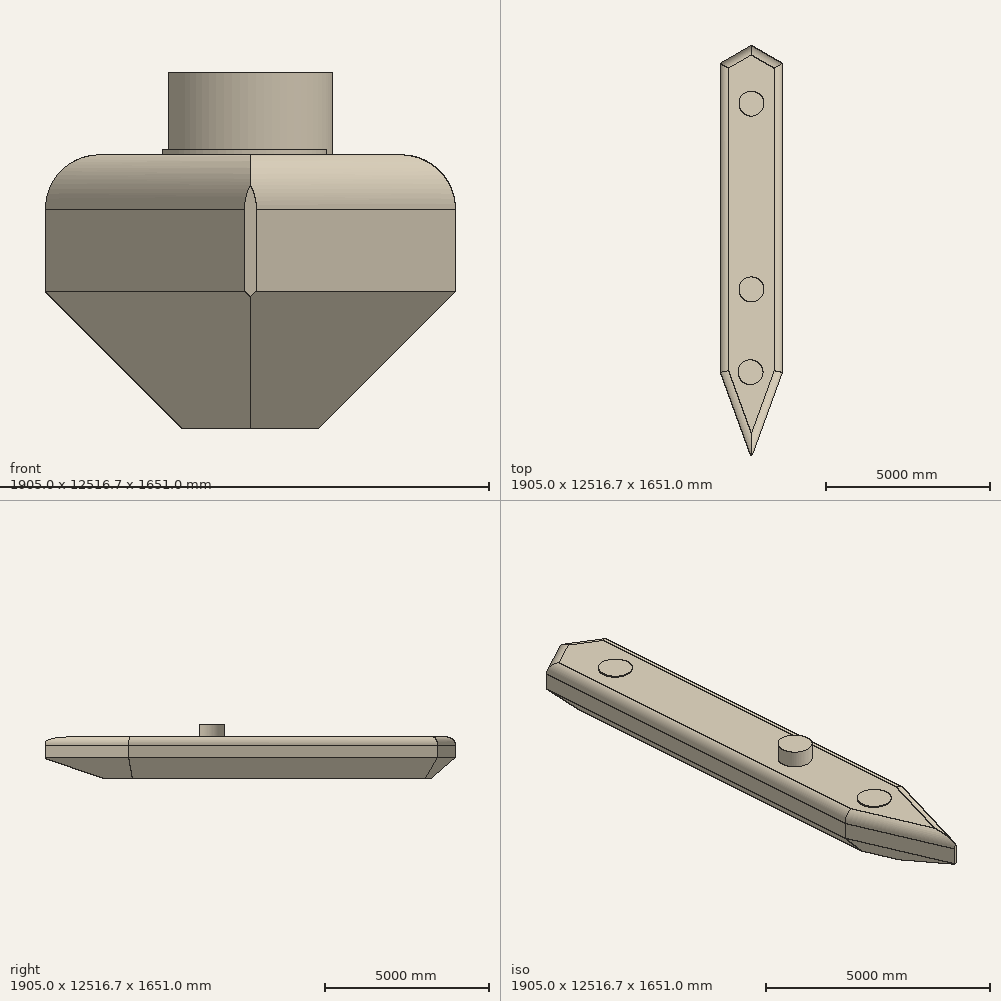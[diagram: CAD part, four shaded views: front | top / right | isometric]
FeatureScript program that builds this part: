
annotation { "Feature Type Name" : "Feature", "Feature Type Description" : "" }
export const myFeature = defineFeature(function(context is Context, id is Id, definition is map)
    precondition{}
    {
        {
            var Q0;
            Q0=qCreatedBy(makeId("Top.planeOp"),FACE);
            var sketch = newSketch(context, id + "F0", { "sketchPlane" : qUnion([Q0])});
            skLineSegment(sketch, "E0.rect.bottom", {"start": v(952.5, -6350) * mm, "end": v(-952.5, -6350) * mm});
            skLineSegment(sketch, "E0.rect.top", {"start": v(952.5, 6350) * mm, "end": v(-952.5, 6350) * mm});
            skLineSegment(sketch, "E0.rect.left", {"start": v(952.5, -6350) * mm, "end": v(952.5, 6350) * mm});
            skLineSegment(sketch, "E0.rect.right", {"start": v(-952.5, -6350) * mm, "end": v(-952.5, 6350) * mm});
            skPoint(sketch, "E0.rect.middle", {"position": v(0, 0) * mm});
            skSolve(sketch);
        }
        {
            var Q0;
            Q0=makeQuery(id+"F0.imprint","IMPRINT",FACE,{"disambiguationData":[TD([[makeQuery(id+"F0.imprint","IMPRINT",EDGE,{"derivedFrom":sQuery(id+"F0.wireOp",EDGE,"E0.rect.bottom")}),-1.0]])]});
            extrude(context, id + "F1", {"entities" : qUnion([Q0]), "depth" : 1270 * mm});
        }
        {
            var Q0;
            Q0=makeQuery(id+"F1.opExtrude","SWEPT_EDGE",EDGE,{"disambiguationData":[OSD([sQuery(id+"F0.wireOp",EDGE,"E0.rect.bottom"),sQuery(id+"F0.wireOp",EDGE,"E0.rect.left")])]});
            var Q1;
            Q1=makeQuery(id+"F1.opExtrude","SWEPT_EDGE",EDGE,{"disambiguationData":[OSD([sQuery(id+"F0.wireOp",EDGE,"E0.rect.bottom"),sQuery(id+"F0.wireOp",EDGE,"E0.rect.right")])]});
            chamfer(context, id + "F2", {"entities" : qUnion([Q0, Q1]), "chamferType" : ChamferType.OFFSET_ANGLE, "width" : 2540 * mm, "oppositeDirection" : false, "angle" : 20 * degree, "tangentPropagation" : true});
        }
        {
            var Q0;
            Q0=makeQuery(id+"F1.opExtrude","SWEPT_EDGE",EDGE,{"disambiguationData":[OSD([sQuery(id+"F0.wireOp",EDGE,"E0.rect.top"),sQuery(id+"F0.wireOp",EDGE,"E0.rect.left")])]});
            var Q1;
            Q1=makeQuery(id+"F1.opExtrude","SWEPT_EDGE",EDGE,{"disambiguationData":[OSD([sQuery(id+"F0.wireOp",EDGE,"E0.rect.top"),sQuery(id+"F0.wireOp",EDGE,"E0.rect.right")])]});
            chamfer(context, id + "F3", {"entities" : qUnion([Q0, Q1]), "chamferType" : ChamferType.OFFSET_ANGLE, "width" : 1270 * mm, "oppositeDirection" : false, "angle" : 30 * degree, "tangentPropagation" : true});
        }
        {
            var Q0;
            Q0=makeQuery(id+"F1.opExtrude","CAP_FACE",FACE,{"disambiguationData":[OSD([sQuery(id+"F0.wireOp",EDGE,"E0.rect.bottom"),sQuery(id+"F0.wireOp",EDGE,"E0.rect.top"),sQuery(id+"F0.wireOp",EDGE,"E0.rect.left"),sQuery(id+"F0.wireOp",EDGE,"E0.rect.right")])],"isStart":false});
            var sketch = newSketch(context, id + "F4", { "sketchPlane" : qUnion([Q0])});
            skCircle(sketch, "E1", {"center": v(0, -1280.4) * mm, "radius": 381 * mm});
            skSolve(sketch);
        }
        {
            var Q0;
            Q0=makeQuery(id+"F4.imprint","IMPRINT",FACE,{"disambiguationData":[TD([[makeQuery(id+"F4.imprint","IMPRINT",EDGE,{"derivedFrom":sQuery(id+"F4.wireOp",EDGE,"E1")}),1.0]])]});
            extrude(context, id + "F5", {"entities" : qUnion([Q0]), "operationType" : NewBodyOperationType.ADD, "depth" : 381 * mm});
        }
        {
            var Q0;
            Q0=makeQuery(id+"F1.opExtrude","CAP_FACE",FACE,{"disambiguationData":[OSD([sQuery(id+"F0.wireOp",EDGE,"E0.rect.bottom"),sQuery(id+"F0.wireOp",EDGE,"E0.rect.top"),sQuery(id+"F0.wireOp",EDGE,"E0.rect.left"),sQuery(id+"F0.wireOp",EDGE,"E0.rect.right")])],"isStart":false});
            var sketch = newSketch(context, id + "F6", { "sketchPlane" : qUnion([Q0])});
            skCircle(sketch, "E2", {"center": v(0, 4389.6) * mm, "radius": 381 * mm});
            skSolve(sketch);
        }
        {
            var Q0;
            Q0=makeQuery(id+"F6.imprint","IMPRINT",FACE,{"disambiguationData":[TD([[makeQuery(id+"F6.imprint","IMPRINT",EDGE,{"derivedFrom":sQuery(id+"F6.wireOp",EDGE,"E2")}),1.0]])]});
            extrude(context, id + "F7", {"entities" : qUnion([Q0]), "operationType" : NewBodyOperationType.ADD, "depth" : 25.4 * mm});
        }
        {
            var Q0;
            Q0=makeQuery(id+"F1.opExtrude","CAP_FACE",FACE,{"disambiguationData":[OSD([sQuery(id+"F0.wireOp",EDGE,"E0.rect.bottom"),sQuery(id+"F0.wireOp",EDGE,"E0.rect.top"),sQuery(id+"F0.wireOp",EDGE,"E0.rect.left"),sQuery(id+"F0.wireOp",EDGE,"E0.rect.right")])],"isStart":false});
            var sketch = newSketch(context, id + "F8", { "sketchPlane" : qUnion([Q0])});
            skCircle(sketch, "E3", {"center": v(-28.02, -3810) * mm, "radius": 381 * mm});
            skSolve(sketch);
        }
        {
            var Q0;
            Q0=makeQuery(id+"F8.imprint","IMPRINT",FACE,{"disambiguationData":[TD([[makeQuery(id+"F8.imprint","IMPRINT",EDGE,{"derivedFrom":sQuery(id+"F8.wireOp",EDGE,"E3")}),1.0]])]});
            extrude(context, id + "F9", {"entities" : qUnion([Q0]), "operationType" : NewBodyOperationType.ADD, "depth" : 25.4 * mm});
        }
        {
            var Q0;
            Q0=makeQuery(id+"F1.opExtrude","CAP_FACE",FACE,{"disambiguationData":[OSD([sQuery(id+"F0.wireOp",EDGE,"E0.rect.bottom"),sQuery(id+"F0.wireOp",EDGE,"E0.rect.top"),sQuery(id+"F0.wireOp",EDGE,"E0.rect.left"),sQuery(id+"F0.wireOp",EDGE,"E0.rect.right")])],"isStart":true});
            chamfer(context, id + "F10", {"entities" : qUnion([Q0]), "width" : 635 * mm, "tangentPropagation" : true});
        }
        {
            var Q0;
            Q0=makeQuery(id+"F1.opExtrude","CAP_EDGE",EDGE,{"disambiguationData":[OSD([sQuery(id+"F0.wireOp",EDGE,"E0.rect.left")])],"isStart":false});
            var Q1;
            {var subQ0=sQuery(id+"F0.wireOp",EDGE,"E0.rect.left");var subQ1=sQuery(id+"F0.wireOp",EDGE,"E0.rect.bottom");Q1=makeQuery(id+"F2.opChamfer","BLEND_EDGE",EDGE,{"blendedFrom":[makeQuery(id+"F1.opExtrude","SWEPT_EDGE",EDGE,{"disambiguationData":[OSD([subQ1,subQ0])]}),makeQuery(id+"F1.opExtrude","CAP_FACE",FACE,{"disambiguationData":[OSD([subQ1,sQuery(id+"F0.wireOp",EDGE,"E0.rect.top"),subQ0,sQuery(id+"F0.wireOp",EDGE,"E0.rect.right")])],"isStart":false})],"blendedInto":[makeQuery(id+"F1.opExtrude","CAP_FACE",FACE,{"disambiguationData":[OSD([subQ1,sQuery(id+"F0.wireOp",EDGE,"E0.rect.top"),subQ0,sQuery(id+"F0.wireOp",EDGE,"E0.rect.right")])],"isStart":false})]});}
            var Q2;
            {var subQ0=sQuery(id+"F0.wireOp",EDGE,"E0.rect.right");var subQ1=sQuery(id+"F0.wireOp",EDGE,"E0.rect.bottom");Q2=makeQuery(id+"F2.opChamfer","BLEND_EDGE",EDGE,{"blendedFrom":[makeQuery(id+"F1.opExtrude","SWEPT_EDGE",EDGE,{"disambiguationData":[OSD([subQ1,subQ0])]}),makeQuery(id+"F1.opExtrude","CAP_FACE",FACE,{"disambiguationData":[OSD([subQ1,sQuery(id+"F0.wireOp",EDGE,"E0.rect.top"),sQuery(id+"F0.wireOp",EDGE,"E0.rect.left"),subQ0])],"isStart":false})],"blendedInto":[makeQuery(id+"F1.opExtrude","CAP_FACE",FACE,{"disambiguationData":[OSD([subQ1,sQuery(id+"F0.wireOp",EDGE,"E0.rect.top"),sQuery(id+"F0.wireOp",EDGE,"E0.rect.left"),subQ0])],"isStart":false})]});}
            var Q3;
            Q3=makeQuery(id+"F1.opExtrude","CAP_EDGE",EDGE,{"disambiguationData":[OSD([sQuery(id+"F0.wireOp",EDGE,"E0.rect.right")])],"isStart":false});
            var Q4;
            {var subQ0=sQuery(id+"F0.wireOp",EDGE,"E0.rect.right");var subQ1=sQuery(id+"F0.wireOp",EDGE,"E0.rect.top");Q4=makeQuery(id+"F3.opChamfer","BLEND_EDGE",EDGE,{"blendedFrom":[makeQuery(id+"F1.opExtrude","SWEPT_EDGE",EDGE,{"disambiguationData":[OSD([subQ1,subQ0])]}),makeQuery(id+"F1.opExtrude","CAP_FACE",FACE,{"disambiguationData":[OSD([sQuery(id+"F0.wireOp",EDGE,"E0.rect.bottom"),subQ1,sQuery(id+"F0.wireOp",EDGE,"E0.rect.left"),subQ0])],"isStart":false})],"blendedInto":[makeQuery(id+"F1.opExtrude","CAP_FACE",FACE,{"disambiguationData":[OSD([sQuery(id+"F0.wireOp",EDGE,"E0.rect.bottom"),subQ1,sQuery(id+"F0.wireOp",EDGE,"E0.rect.left"),subQ0])],"isStart":false})]});}
            var Q5;
            {var subQ0=sQuery(id+"F0.wireOp",EDGE,"E0.rect.left");var subQ1=sQuery(id+"F0.wireOp",EDGE,"E0.rect.top");Q5=makeQuery(id+"F3.opChamfer","BLEND_EDGE",EDGE,{"blendedFrom":[makeQuery(id+"F1.opExtrude","SWEPT_EDGE",EDGE,{"disambiguationData":[OSD([subQ1,subQ0])]}),makeQuery(id+"F1.opExtrude","CAP_FACE",FACE,{"disambiguationData":[OSD([sQuery(id+"F0.wireOp",EDGE,"E0.rect.bottom"),subQ1,subQ0,sQuery(id+"F0.wireOp",EDGE,"E0.rect.right")])],"isStart":false})],"blendedInto":[makeQuery(id+"F1.opExtrude","CAP_FACE",FACE,{"disambiguationData":[OSD([sQuery(id+"F0.wireOp",EDGE,"E0.rect.bottom"),subQ1,subQ0,sQuery(id+"F0.wireOp",EDGE,"E0.rect.right")])],"isStart":false})]});}
            fillet(context, id + "F11", {"entities" : qUnion([Q0, Q1, Q2, Q3, Q4, Q5]), "radius" : 254 * mm, "tangentPropagation" : true, "allowEdgeOverflow" : false});
        }
    });
